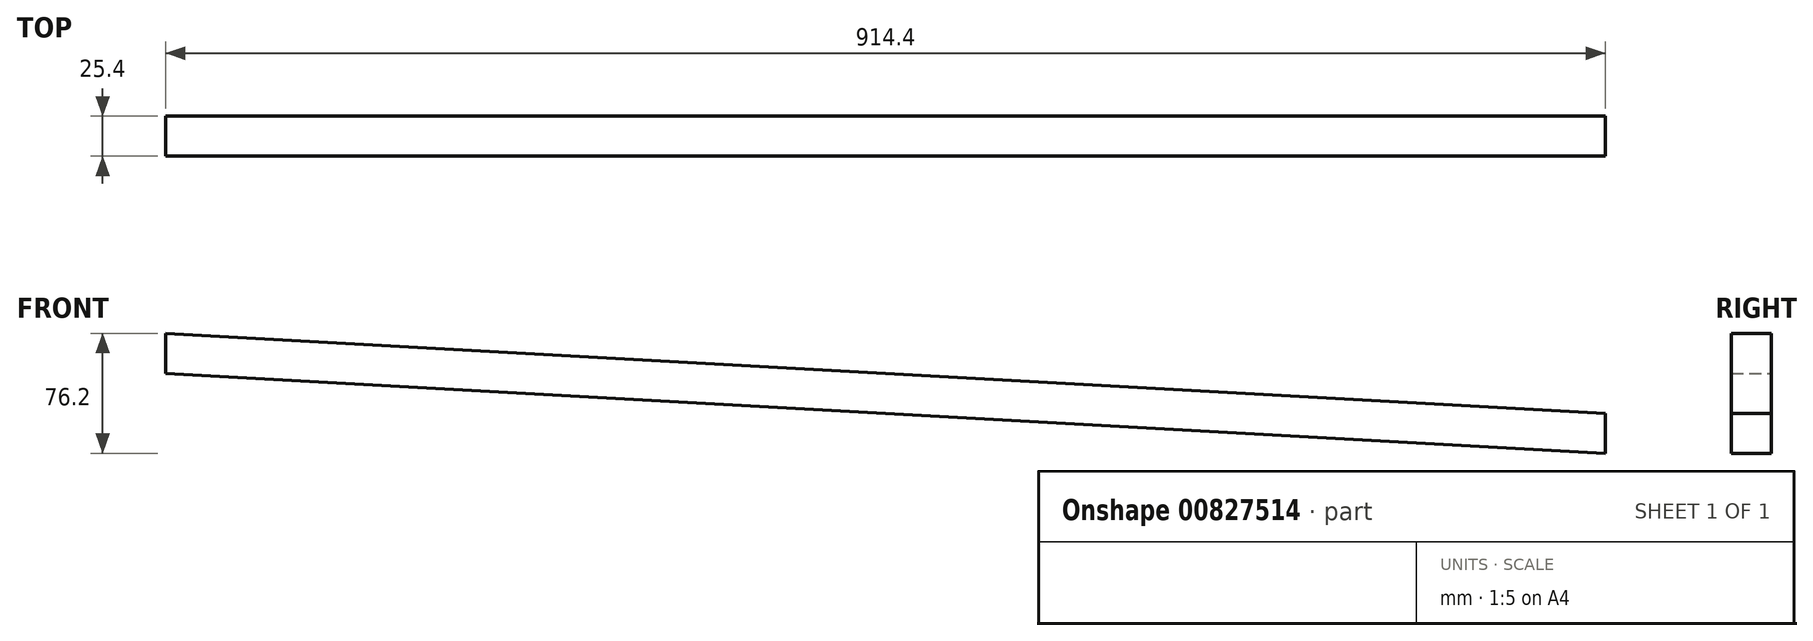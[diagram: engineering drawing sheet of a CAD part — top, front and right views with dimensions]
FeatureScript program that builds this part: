
annotation { "Feature Type Name" : "Feature", "Feature Type Description" : "" }
export const myFeature = defineFeature(function(context is Context, id is Id, definition is map)
    precondition{}
    {
        {
            var Q0;
            Q0=qCreatedBy(makeId("Front.planeOp"),FACE);
            var sketch = newSketch(context, id + "F0", { "sketchPlane" : qUnion([Q0])});
            skLineSegment(sketch, "E0", {"start": v(-457.2, 970.77) * mm, "end": v(-457.2, -45.23) * mm, "construction": true});
            skLineSegment(sketch, "E1", {"start": v(457.2, -45.23) * mm, "end": v(457.2, 919.97) * mm, "construction": true});
            skLineSegment(sketch, "E2", {"start": v(-457.2, 970.77) * mm, "end": v(457.2, 919.97) * mm});
            skLineSegment(sketch, "E3", {"start": v(-457.2, 945.37) * mm, "end": v(457.2, 894.57) * mm});
            skLineSegment(sketch, "E4", {"start": v(457.2, 919.97) * mm, "end": v(457.2, 894.57) * mm});
            skLineSegment(sketch, "E5", {"start": v(-457.2, 970.77) * mm, "end": v(-457.2, 945.37) * mm});
            skSolve(sketch);
        }
        {
            var Q0;
            Q0=makeQuery(id+"F0.imprint","IMPRINT",FACE,{"disambiguationData":[TD([[makeQuery(id+"F0.imprint","IMPRINT",EDGE,{"derivedFrom":sQuery(id+"F0.wireOp",EDGE,"E2")}),-1.0]])]});
            extrude(context, id + "F1", {"entities" : qUnion([Q0]), "depth" : 25.4 * mm, "offsetDistance" : 25.4 * mm});
        }
    });
